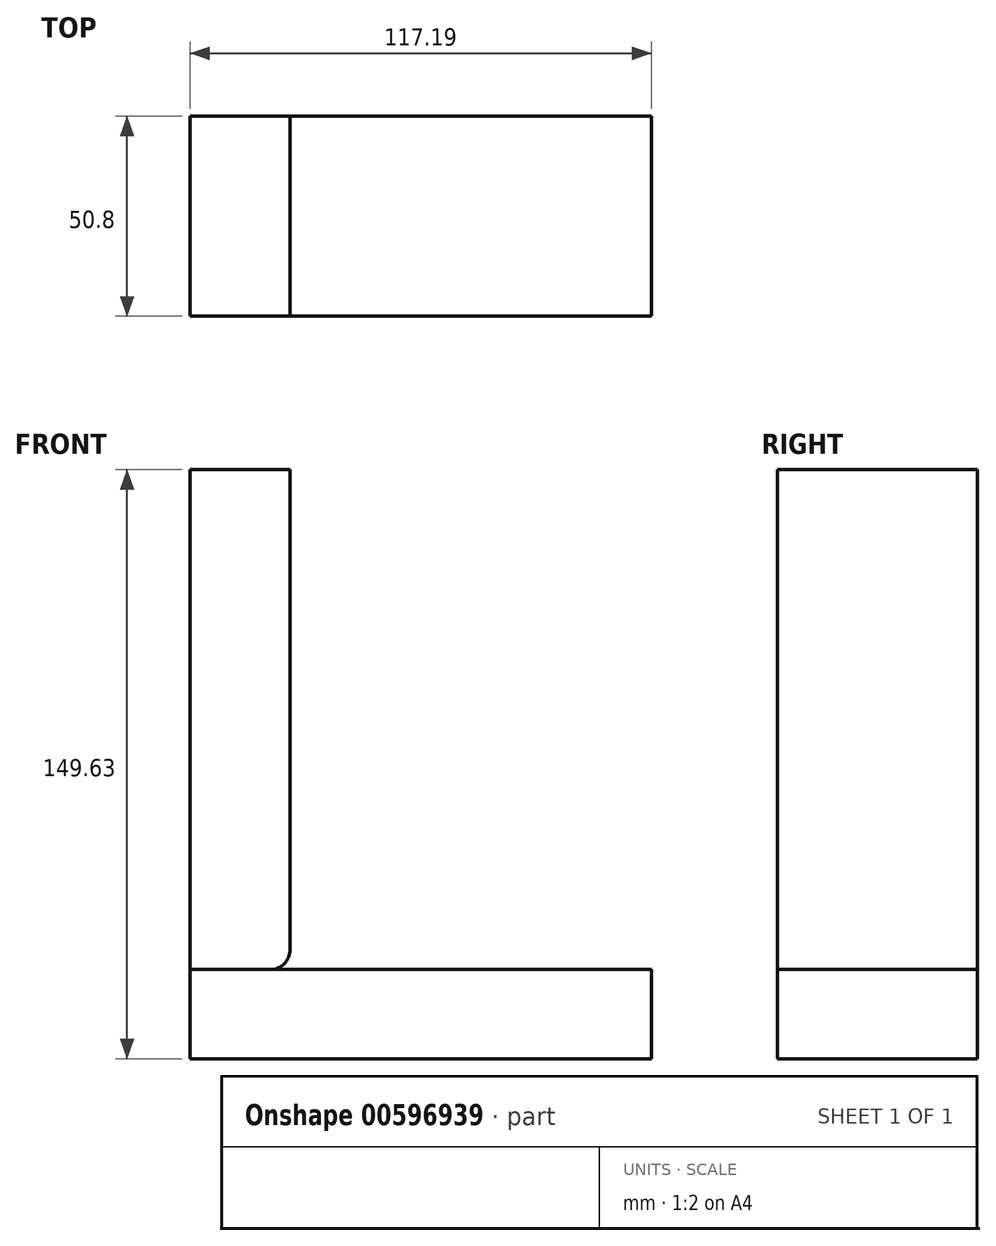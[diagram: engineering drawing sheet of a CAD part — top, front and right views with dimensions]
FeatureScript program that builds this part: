
annotation { "Feature Type Name" : "Feature", "Feature Type Description" : "" }
export const myFeature = defineFeature(function(context is Context, id is Id, definition is map)
    precondition{}
    {
        {
            var Q0;
            Q0=qCreatedBy(makeId("Front.planeOp"),FACE);
            var sketch = newSketch(context, id + "F0", { "sketchPlane" : qUnion([Q0])});
            skLineSegment(sketch, "E0.bottom", {"start": v(0, 127) * mm, "end": v(-25.4, 127) * mm});
            skLineSegment(sketch, "E0.top", {"start": v(0, 0) * mm, "end": v(-25.4, 0) * mm});
            skLineSegment(sketch, "E0.left", {"start": v(0, 127) * mm, "end": v(0, 0) * mm});
            skLineSegment(sketch, "E0.right", {"start": v(-25.4, 127) * mm, "end": v(-25.4, 0) * mm});
            skLineSegment(sketch, "E1.bottom", {"start": v(-25.4, 0) * mm, "end": v(91.79, 0) * mm});
            skLineSegment(sketch, "E1.top", {"start": v(-25.4, -22.63) * mm, "end": v(91.79, -22.63) * mm});
            skLineSegment(sketch, "E1.left", {"start": v(-25.4, 0) * mm, "end": v(-25.4, -22.63) * mm});
            skLineSegment(sketch, "E1.right", {"start": v(91.79, 0) * mm, "end": v(91.79, -22.63) * mm});
            skSolve(sketch);
        }
        {
            var Q0;
            Q0=makeQuery(id+"F0.imprint","IMPRINT",FACE,{"disambiguationData":[TD([[makeQuery(id+"F0.imprint","IMPRINT",EDGE,{"derivedFrom":sQuery(id+"F0.wireOp",EDGE,"E0.bottom")}),1.0]])]});
            extrude(context, id + "F1", {"entities" : qUnion([Q0]), "endBound" : BoundingType.SYMMETRIC, "depth" : 50.8 * mm, "offsetDistance" : 25.4 * mm});
        }
        {
            var Q0;
            Q0=makeQuery(id+"F0.imprint","IMPRINT",FACE,{"disambiguationData":[TD([[makeQuery(id+"F0.imprint","IMPRINT",EDGE,{"derivedFrom":sQuery(id+"F0.wireOp",EDGE,"E1.top")}),1.0]])]});
            var Q1;
            Q1=makeQuery(id+"F1.opExtrude","CAP_FACE",FACE,{"disambiguationData":[OSD([sQuery(id+"F0.wireOp",EDGE,"E0.bottom"),sQuery(id+"F0.wireOp",EDGE,"E0.left"),sQuery(id+"F0.wireOp",EDGE,"E0.right"),sQuery(id+"F0.wireOp",EDGE,"E1.bottom")])],"isStart":false});
            var Q2;
            Q2=makeQuery(id+"F1.opExtrude","CAP_FACE",FACE,{"disambiguationData":[OSD([sQuery(id+"F0.wireOp",EDGE,"E0.bottom"),sQuery(id+"F0.wireOp",EDGE,"E0.left"),sQuery(id+"F0.wireOp",EDGE,"E0.right"),sQuery(id+"F0.wireOp",EDGE,"E1.bottom")])],"isStart":true});
            extrude(context, id + "F2", {"entities" : qUnion([Q0]), "endBound" : BoundingType.UP_TO_SURFACE, "depth" : 25.4 * mm, "endBoundEntityFace" : qUnion([Q1]), "offsetDistance" : 25.4 * mm, "hasSecondDirection" : true, "secondDirectionBound" : SecondDirectionBoundingType.UP_TO_SURFACE, "secondDirectionOppositeDirection" : true, "secondDirectionDepth" : 25.4 * mm, "secondDirectionBoundEntityFace" : qUnion([Q2])});
        }
        {
            var Q0;
            Q0=makeQuery(id+"F1.opExtrude","SWEPT_EDGE",EDGE,{"disambiguationData":[OSD([sQuery(id+"F0.wireOp",EDGE,"E0.left"),sQuery(id+"F0.wireOp",EDGE,"E1.bottom")])]});
            fillet(context, id + "F3", {"entities" : qUnion([Q0]), "radius" : 5.08 * mm, "tangentPropagation" : true, "allowEdgeOverflow" : false});
        }
    });
